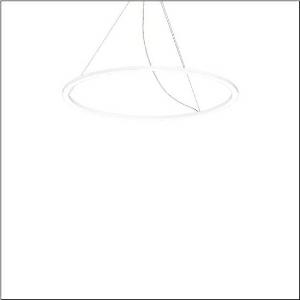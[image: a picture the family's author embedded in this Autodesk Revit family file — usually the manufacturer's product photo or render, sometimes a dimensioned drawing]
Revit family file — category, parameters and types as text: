
# Revit family: silica_r__21_ring-d_5pjbd3d3004a_4211
name_source: partatom
category: Lighting Fixtures
units: mm (PartAtom-declared; Revit-internal decimal feet)

## family parameters
Cut with Voids When Loaded = No
Host = Face
Light Source = No
Part Type = Normal
Room Calculation Point = No
Round Connector Dimension = Use Diameter
Shared = No

## types (1)
- Silica® 21 Ring-D (1 x LED, 8420 lm, 94 W, 4000K)
    Apparent Load = 94 VA
    CIE Flux Codes = 37 69 92 100 100
    Color Rendering = 80
    Color Temperature = 4000K
    Default Elevation = 1800 mm
    Description = Silica® 21 Ring-D, suspended luminaire, of PMMA, frosted, light emission: ring underside luminous distribution, primary light characteristic: symmetric, installation type: suspended mounting, LED, rated luminous flux: 8.420lm, luminous efficacy: 90lm/W, light colour: 840, colour temperature: 4000K, control gear: DALI 2, with terminal, 5-pole, mains connection: 230V, AC/DC, 0/50..60Hz, rated input power: 94W, housing, of extruded aluminium section, traffic white (RAL 9016), diameter: 1.100mm, ceiling canopy, traffic white (RAL 9016), protection rating (lamp compartment): IP40, insulation class (complete): insulation class I (protective earthing), certification: CE, impact resistance: IK02, permissible operating ambient temperature: 0..+35°C, packaging unit: 1 piece
    Height = 25 mm  [stored 0.082021 ft]
    Lamp = 1 x LED
    Lamp Light Flux = 8420 lm
    Lamp Power = 94 W
    Lamp count = 1
    Length = 1100 mm
    Luminous efficacy = 90 lm/W
    Manufacturer = Siteco
    ModVariant = No
    Model = 5PJBD3D3004A
    Mounting Place = Ceiling
    Mounting Type = Pendant
    Number of Poles = 1
    OnlyDefault = Yes
    Power Factor = 1
    Product Name = Silica® 21 Ring-D
    Product group = suspended luminaire
    ProductGroupID = 905
    Protection Class = Protection class I
    Protection Degree = IP 40
    RLX_Detail_Level = 1
    RLX_Emergency_Light_Flux = 0 lm
    RLX_Emergency_Type = 0
    RLX_Emergency_Type_DB = No
    RlxData = <blob elided: 12513 chars, md5=d67f31e8>
    Socket = socket
    Standby Power = 0 W
    System Light Flux = 8420 lm
    System Power = 94 W
    Type Comments = Product without accessories
    Type Image = l_1258355.jpg
    URL = http://relux.com
    VarID = ---
    Voltage = 0 V
    Weight = 0.00 kg
    Width = 0 mm  [stored 0 ft]

note: [stored X ft] marks values corroborated as IEEE doubles in the binary element streams (Revit-internal decimal feet)

## geometry (parser evidence)
native form markers: Sweep x9
no freeform markers — native parametric forms only
